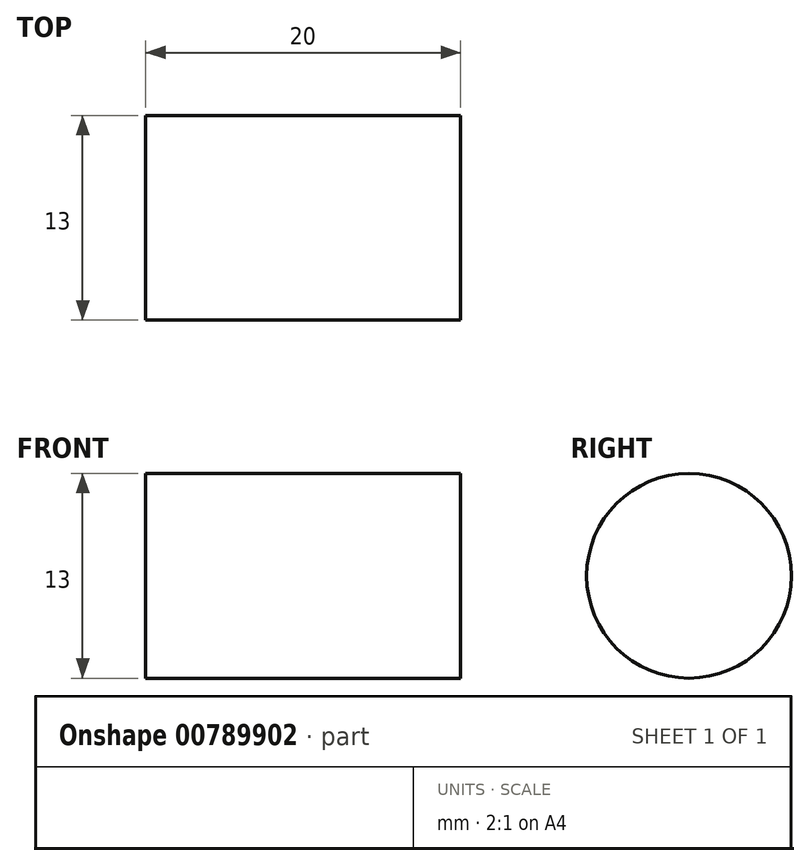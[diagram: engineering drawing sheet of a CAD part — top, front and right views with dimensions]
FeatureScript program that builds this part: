
annotation { "Feature Type Name" : "Feature", "Feature Type Description" : "" }
export const myFeature = defineFeature(function(context is Context, id is Id, definition is map)
    precondition{}
    {
        {
            var Q0;
            Q0=qCreatedBy(makeId("Right.planeOp"),FACE);
            var sketch = newSketch(context, id + "F0", { "sketchPlane" : qUnion([Q0])});
            skCircle(sketch, "E0", {"center": v(2086.78, 2239.07) * mm, "radius": 50 * mm, "construction": true});
            skCircle(sketch, "E1", {"center": v(2351, 2449) * mm, "radius": 2.12 * mm, "construction": true});
            skCircle(sketch, "E2", {"center": v(2325.71, 2465.14) * mm, "radius": 2.12 * mm, "construction": true});
            skCircle(sketch, "E3", {"center": v(2435.8, 2760.38) * mm, "radius": 2.12 * mm, "construction": true});
            skCircle(sketch, "E4", {"center": v(2431.3, 2790.04) * mm, "radius": 2.12 * mm, "construction": true});
            skCircle(sketch, "E5", {"center": v(2579.07, 2770.86) * mm, "radius": 5.5 * mm, "construction": true});
            skCircle(sketch, "E6", {"center": v(2661.57, 2688.36) * mm, "radius": 5.5 * mm, "construction": true});
            skCircle(sketch, "E7", {"center": v(2637.4, 2746.7) * mm, "radius": 5.5 * mm, "construction": true});
            skCircle(sketch, "E8", {"center": v(2520.73, 2746.7) * mm, "radius": 5.5 * mm, "construction": true});
            skCircle(sketch, "E9", {"center": v(2520.73, 2630.03) * mm, "radius": 5.5 * mm, "construction": true});
            skCircle(sketch, "E10", {"center": v(2496.57, 2688.36) * mm, "radius": 5.5 * mm, "construction": true});
            skCircle(sketch, "E11", {"center": v(2579.07, 2605.86) * mm, "radius": 5.5 * mm, "construction": true});
            skCircle(sketch, "E12", {"center": v(2637.4, 2630.03) * mm, "radius": 5.5 * mm, "construction": true});
            skCircle(sketch, "E13", {"center": v(2427.07, 2409.36) * mm, "radius": 10 * mm, "construction": true});
            skCircle(sketch, "E14", {"center": v(2622.07, 2789.36) * mm, "radius": 11 * mm, "construction": true});
            skCircle(sketch, "E15", {"center": v(2652.07, 2789.36) * mm, "radius": 6.5 * mm, "construction": true});
            skCircle(sketch, "E16", {"center": v(2102.07, 2789.36) * mm, "radius": 6.5 * mm, "construction": true});
            skCircle(sketch, "E17", {"center": v(2102.07, 2394.36) * mm, "radius": 6.5 * mm, "construction": true});
            skCircle(sketch, "E18", {"center": v(2217.07, 2764.36) * mm, "radius": 4.5 * mm, "construction": true});
            skArc(sketch, "E19", {"start": v(2079.57, 2594.36) * mm, "mid": v(2077.8, 2590.1) * mm, "end": v(2082.07, 2591.86) * mm, "construction": true});
            skLineSegment(sketch, "E20", {"start": v(2075.94, 2591.86) * mm, "end": v(2083.2, 2591.86) * mm, "construction": true});
            skLineSegment(sketch, "E21", {"start": v(2079.57, 2595.49) * mm, "end": v(2079.57, 2588.24) * mm, "construction": true});
            skCircle(sketch, "E22", {"center": v(2079.57, 2591.86) * mm, "radius": 2.12 * mm, "construction": true});
            skArc(sketch, "E23", {"start": v(2084.7, 2379.49) * mm, "mid": v(2082.92, 2375.22) * mm, "end": v(2087.2, 2376.99) * mm, "construction": true});
            skLineSegment(sketch, "E24", {"start": v(2081.07, 2376.99) * mm, "end": v(2088.32, 2376.99) * mm, "construction": true});
            skLineSegment(sketch, "E25", {"start": v(2084.7, 2380.61) * mm, "end": v(2084.7, 2373.36) * mm, "construction": true});
            skCircle(sketch, "E26", {"center": v(2084.7, 2376.99) * mm, "radius": 2.12 * mm, "construction": true});
            skArc(sketch, "E27", {"start": v(2463.4, 2375.7) * mm, "mid": v(2461.64, 2371.43) * mm, "end": v(2465.9, 2373.2) * mm, "construction": true});
            skLineSegment(sketch, "E28", {"start": v(2459.78, 2373.2) * mm, "end": v(2467.03, 2373.2) * mm, "construction": true});
            skLineSegment(sketch, "E29", {"start": v(2463.4, 2376.82) * mm, "end": v(2463.4, 2369.57) * mm, "construction": true});
            skCircle(sketch, "E30", {"center": v(2463.4, 2373.2) * mm, "radius": 2.12 * mm, "construction": true});
            skArc(sketch, "E31", {"start": v(2569.26, 2479.66) * mm, "mid": v(2567.5, 2475.4) * mm, "end": v(2571.76, 2477.16) * mm, "construction": true});
            skLineSegment(sketch, "E32", {"start": v(2565.64, 2477.16) * mm, "end": v(2572.89, 2477.16) * mm, "construction": true});
            skLineSegment(sketch, "E33", {"start": v(2569.26, 2480.79) * mm, "end": v(2569.26, 2473.54) * mm, "construction": true});
            skCircle(sketch, "E34", {"center": v(2569.26, 2477.16) * mm, "radius": 2.12 * mm, "construction": true});
            skArc(sketch, "E35", {"start": v(2673.23, 2585.52) * mm, "mid": v(2671.47, 2581.25) * mm, "end": v(2675.73, 2583.02) * mm, "construction": true});
            skLineSegment(sketch, "E36", {"start": v(2669.6, 2583.02) * mm, "end": v(2676.86, 2583.02) * mm, "construction": true});
            skLineSegment(sketch, "E37", {"start": v(2673.23, 2586.64) * mm, "end": v(2673.23, 2579.4) * mm, "construction": true});
            skCircle(sketch, "E38", {"center": v(2673.23, 2583.02) * mm, "radius": 2.12 * mm, "construction": true});
            skArc(sketch, "E39", {"start": v(2669.44, 2809.24) * mm, "mid": v(2667.67, 2804.97) * mm, "end": v(2671.94, 2806.74) * mm, "construction": true});
            skLineSegment(sketch, "E40", {"start": v(2665.81, 2806.74) * mm, "end": v(2673.06, 2806.74) * mm, "construction": true});
            skLineSegment(sketch, "E41", {"start": v(2669.44, 2810.36) * mm, "end": v(2669.44, 2803.11) * mm, "construction": true});
            skCircle(sketch, "E42", {"center": v(2669.44, 2806.74) * mm, "radius": 2.12 * mm, "construction": true});
            skArc(sketch, "E43", {"start": v(2474.44, 2814.36) * mm, "mid": v(2472.67, 2810.1) * mm, "end": v(2476.94, 2811.86) * mm, "construction": true});
            skLineSegment(sketch, "E44", {"start": v(2470.81, 2811.86) * mm, "end": v(2478.06, 2811.86) * mm, "construction": true});
            skLineSegment(sketch, "E45", {"start": v(2474.44, 2815.49) * mm, "end": v(2474.44, 2808.24) * mm, "construction": true});
            skCircle(sketch, "E46", {"center": v(2474.44, 2811.86) * mm, "radius": 2.12 * mm, "construction": true});
            skArc(sketch, "E47", {"start": v(2279.7, 2814.36) * mm, "mid": v(2277.92, 2810.1) * mm, "end": v(2282.2, 2811.86) * mm, "construction": true});
            skLineSegment(sketch, "E48", {"start": v(2276.07, 2811.86) * mm, "end": v(2283.32, 2811.86) * mm, "construction": true});
            skLineSegment(sketch, "E49", {"start": v(2279.7, 2815.49) * mm, "end": v(2279.7, 2808.24) * mm, "construction": true});
            skCircle(sketch, "E50", {"center": v(2279.7, 2811.86) * mm, "radius": 2.12 * mm, "construction": true});
            skArc(sketch, "E51", {"start": v(2084.7, 2809.24) * mm, "mid": v(2082.92, 2804.97) * mm, "end": v(2087.2, 2806.74) * mm, "construction": true});
            skLineSegment(sketch, "E52", {"start": v(2081.07, 2806.74) * mm, "end": v(2088.32, 2806.74) * mm, "construction": true});
            skLineSegment(sketch, "E53", {"start": v(2084.7, 2810.36) * mm, "end": v(2084.7, 2803.11) * mm, "construction": true});
            skCircle(sketch, "E54", {"center": v(2084.7, 2806.74) * mm, "radius": 2.12 * mm, "construction": true});
            skCircle(sketch, "E55", {"center": v(2579.07, 2688.36) * mm, "radius": 55 * mm, "construction": true});
            skLineSegment(sketch, "E56", {"start": v(2318.05, 2494.04) * mm, "end": v(2326.48, 2488.66) * mm, "construction": true});
            skArc(sketch, "E57", {"start": v(2323.13, 2496.43) * mm, "mid": v(2320.87, 2496.83) * mm, "end": v(2319, 2495.51) * mm, "construction": true});
            skLineSegment(sketch, "E58", {"start": v(2327.7, 2490.56) * mm, "end": v(2319.63, 2477.91) * mm, "construction": true});
            skLineSegment(sketch, "E59", {"start": v(2296.28, 2459.9) * mm, "end": v(2304.7, 2454.51) * mm, "construction": true});
            skArc(sketch, "E60", {"start": v(2295.34, 2458.42) * mm, "mid": v(2294.94, 2456.15) * mm, "end": v(2296.25, 2454.27) * mm, "construction": true});
            skLineSegment(sketch, "E61", {"start": v(2311.56, 2465.26) * mm, "end": v(2303.5, 2452.62) * mm, "construction": true});
            skLineSegment(sketch, "E62", {"start": v(2295.34, 2458.42) * mm, "end": v(2319, 2495.51) * mm, "construction": true});
            skLineSegment(sketch, "E63", {"start": v(2301.92, 2468.74) * mm, "end": v(2310.35, 2463.37) * mm, "construction": true});
            skLineSegment(sketch, "E64", {"start": v(2312.4, 2485.19) * mm, "end": v(2320.84, 2479.8) * mm, "construction": true});
            skLineSegment(sketch, "E65", {"start": v(2319.63, 2477.91) * mm, "end": v(2358.41, 2453.18) * mm, "construction": true});
            skLineSegment(sketch, "E66", {"start": v(2327.7, 2490.56) * mm, "end": v(2366.48, 2465.83) * mm, "construction": true});
            skLineSegment(sketch, "E67", {"start": v(2323.13, 2496.43) * mm, "end": v(2368.67, 2467.4) * mm, "construction": true});
            skLineSegment(sketch, "E68", {"start": v(2358.41, 2453.18) * mm, "end": v(2366.48, 2465.83) * mm, "construction": true});
            skArc(sketch, "E69", {"start": v(2369.58, 2463.26) * mm, "mid": v(2369.98, 2465.52) * mm, "end": v(2368.67, 2467.4) * mm, "construction": true});
            skLineSegment(sketch, "E70", {"start": v(2342.28, 2427.89) * mm, "end": v(2350.35, 2440.53) * mm, "construction": true});
            skLineSegment(sketch, "E71", {"start": v(2303.5, 2452.62) * mm, "end": v(2342.28, 2427.89) * mm, "construction": true});
            skLineSegment(sketch, "E72", {"start": v(2311.56, 2465.26) * mm, "end": v(2350.35, 2440.53) * mm, "construction": true});
            skLineSegment(sketch, "E73", {"start": v(2296.25, 2454.27) * mm, "end": v(2341.78, 2425.24) * mm, "construction": true});
            skLineSegment(sketch, "E74", {"start": v(2345.93, 2426.16) * mm, "end": v(2369.58, 2463.26) * mm, "construction": true});
            skArc(sketch, "E75", {"start": v(2341.78, 2425.24) * mm, "mid": v(2344.04, 2424.84) * mm, "end": v(2345.93, 2426.16) * mm, "construction": true});
            skLineSegment(sketch, "E76", {"start": v(2419.07, 2735.6) * mm, "end": v(2417.57, 2745.49) * mm, "construction": true});
            skArc(sketch, "E77", {"start": v(2413.92, 2737.85) * mm, "mid": v(2415.1, 2735.89) * mm, "end": v(2417.33, 2735.34) * mm, "construction": true});
            skLineSegment(sketch, "E78", {"start": v(2415.34, 2745.15) * mm, "end": v(2430.17, 2747.4) * mm, "construction": true});
            skLineSegment(sketch, "E79", {"start": v(2459.1, 2741.66) * mm, "end": v(2457.61, 2751.55) * mm, "construction": true});
            skArc(sketch, "E80", {"start": v(2460.84, 2741.93) * mm, "mid": v(2462.8, 2743.11) * mm, "end": v(2463.36, 2745.34) * mm, "construction": true});
            skLineSegment(sketch, "E81", {"start": v(2445, 2749.64) * mm, "end": v(2459.83, 2751.89) * mm, "construction": true});
            skLineSegment(sketch, "E82", {"start": v(2460.84, 2741.93) * mm, "end": v(2417.33, 2735.34) * mm, "construction": true});
            skLineSegment(sketch, "E83", {"start": v(2448.73, 2740.1) * mm, "end": v(2447.23, 2749.98) * mm, "construction": true});
            skLineSegment(sketch, "E84", {"start": v(2429.45, 2737.17) * mm, "end": v(2427.95, 2747.06) * mm, "construction": true});
            skLineSegment(sketch, "E85", {"start": v(2430.17, 2747.4) * mm, "end": v(2423.28, 2792.88) * mm, "construction": true});
            skLineSegment(sketch, "E86", {"start": v(2415.34, 2745.15) * mm, "end": v(2408.45, 2790.63) * mm, "construction": true});
            skLineSegment(sketch, "E87", {"start": v(2413.92, 2737.85) * mm, "end": v(2405.83, 2791.24) * mm, "construction": true});
            skLineSegment(sketch, "E88", {"start": v(2423.28, 2792.88) * mm, "end": v(2408.45, 2790.63) * mm, "construction": true});
            skArc(sketch, "E89", {"start": v(2408.35, 2794.66) * mm, "mid": v(2406.38, 2793.47) * mm, "end": v(2405.83, 2791.24) * mm, "construction": true});
            skLineSegment(sketch, "E90", {"start": v(2452.94, 2797.37) * mm, "end": v(2438.11, 2795.12) * mm, "construction": true});
            skLineSegment(sketch, "E91", {"start": v(2459.83, 2751.89) * mm, "end": v(2452.94, 2797.37) * mm, "construction": true});
            skLineSegment(sketch, "E92", {"start": v(2445, 2749.64) * mm, "end": v(2438.11, 2795.12) * mm, "construction": true});
            skLineSegment(sketch, "E93", {"start": v(2463.36, 2745.34) * mm, "end": v(2455.27, 2798.73) * mm, "construction": true});
            skLineSegment(sketch, "E94", {"start": v(2451.85, 2801.25) * mm, "end": v(2408.35, 2794.66) * mm, "construction": true});
            skArc(sketch, "E95", {"start": v(2455.27, 2798.73) * mm, "mid": v(2454.08, 2800.7) * mm, "end": v(2451.85, 2801.25) * mm, "construction": true});
            skArc(sketch, "E96", {"start": v(2207.17, 2779.23) * mm, "mid": v(2162.07, 2764.36) * mm, "end": v(2207.17, 2749.5) * mm, "construction": true});
            skCircle(sketch, "E97", {"center": v(2187.07, 2764.36) * mm, "radius": 14 * mm, "construction": true});
            skLineSegment(sketch, "E98", {"start": v(2484.93, 2814.36) * mm, "end": v(2657.07, 2814.36) * mm, "construction": true});
            skLineSegment(sketch, "E99", {"start": v(2290.18, 2814.36) * mm, "end": v(2463.95, 2814.36) * mm, "construction": true});
            skArc(sketch, "E100", {"start": v(2466.95, 2811.5) * mm, "mid": v(2474.44, 2804.36) * mm, "end": v(2481.93, 2811.5) * mm, "construction": true});
            skArc(sketch, "E101", {"start": v(2484.93, 2814.36) * mm, "mid": v(2482.86, 2813.53) * mm, "end": v(2481.93, 2811.5) * mm, "construction": true});
            skArc(sketch, "E102", {"start": v(2466.95, 2811.5) * mm, "mid": v(2466.02, 2813.53) * mm, "end": v(2463.95, 2814.36) * mm, "construction": true});
            skArc(sketch, "E103", {"start": v(2272.2, 2811.5) * mm, "mid": v(2271.27, 2813.53) * mm, "end": v(2269.2, 2814.36) * mm, "construction": true});
            skArc(sketch, "E104", {"start": v(2290.18, 2814.36) * mm, "mid": v(2288.1, 2813.53) * mm, "end": v(2287.18, 2811.5) * mm, "construction": true});
            skArc(sketch, "E105", {"start": v(2285.24, 2806.81) * mm, "mid": v(2286.62, 2809) * mm, "end": v(2287.18, 2811.5) * mm, "construction": true});
            skArc(sketch, "E106", {"start": v(2272.2, 2811.5) * mm, "mid": v(2279.7, 2804.36) * mm, "end": v(2287.18, 2811.5) * mm, "construction": true});
            skLineSegment(sketch, "E107", {"start": v(2455.9, 2373.2) * mm, "end": v(2455.9, 2372.36) * mm, "construction": true});
            skLineSegment(sketch, "E108", {"start": v(2092.2, 2376.99) * mm, "end": v(2092.2, 2372.36) * mm, "construction": true});
            skArc(sketch, "E109", {"start": v(2574.3, 2482.71) * mm, "mid": v(2563.96, 2482.47) * mm, "end": v(2563.71, 2472.12) * mm, "construction": true});
            skLineSegment(sketch, "E110", {"start": v(2077.07, 2510.77) * mm, "end": v(2077.07, 2389.36) * mm, "construction": true});
            skLineSegment(sketch, "E111", {"start": v(2077.07, 2714.11) * mm, "end": v(2077.07, 2602.35) * mm, "construction": true});
            skArc(sketch, "E112", {"start": v(2662.63, 2809.87) * mm, "mid": v(2662.55, 2812.52) * mm, "end": v(2660.4, 2814.08) * mm, "construction": true});
            skArc(sketch, "E113", {"start": v(2676.79, 2797.7) * mm, "mid": v(2675.23, 2799.85) * mm, "end": v(2672.57, 2799.92) * mm, "construction": true});
            skArc(sketch, "E114", {"start": v(2660.4, 2814.08) * mm, "mid": v(2658.74, 2814.3) * mm, "end": v(2657.07, 2814.36) * mm, "construction": true});
            skArc(sketch, "E115", {"start": v(2662.63, 2809.87) * mm, "mid": v(2664.14, 2801.43) * mm, "end": v(2672.57, 2799.92) * mm, "construction": true});
            skArc(sketch, "E116", {"start": v(2677.07, 2794.36) * mm, "mid": v(2677, 2796.04) * mm, "end": v(2676.79, 2797.7) * mm, "construction": true});
            skArc(sketch, "E117", {"start": v(2682.07, 2794.36) * mm, "mid": v(2674.74, 2812.04) * mm, "end": v(2657.07, 2819.36) * mm, "construction": true});
            skArc(sketch, "E118", {"start": v(2079.92, 2584.37) * mm, "mid": v(2077.9, 2583.44) * mm, "end": v(2077.07, 2581.37) * mm, "construction": true});
            skArc(sketch, "E119", {"start": v(2077.07, 2602.35) * mm, "mid": v(2077.9, 2600.28) * mm, "end": v(2079.92, 2599.35) * mm, "construction": true});
            skLineSegment(sketch, "E120", {"start": v(2077.07, 2581.37) * mm, "end": v(2077.07, 2510.77) * mm, "construction": true});
            skArc(sketch, "E121", {"start": v(2079.92, 2584.37) * mm, "mid": v(2087.07, 2591.86) * mm, "end": v(2079.92, 2599.35) * mm, "construction": true});
            skArc(sketch, "E122", {"start": v(2097.07, 2819.36) * mm, "mid": v(2079.39, 2812.04) * mm, "end": v(2072.07, 2794.36) * mm, "construction": true});
            skArc(sketch, "E123", {"start": v(2077.35, 2797.7) * mm, "mid": v(2077.14, 2796.04) * mm, "end": v(2077.07, 2794.36) * mm, "construction": true});
            skArc(sketch, "E124", {"start": v(2081.56, 2799.92) * mm, "mid": v(2090, 2801.43) * mm, "end": v(2091.5, 2809.87) * mm, "construction": true});
            skArc(sketch, "E125", {"start": v(2097.07, 2814.36) * mm, "mid": v(2095.4, 2814.3) * mm, "end": v(2093.73, 2814.08) * mm, "construction": true});
            skArc(sketch, "E126", {"start": v(2081.56, 2799.92) * mm, "mid": v(2078.9, 2799.85) * mm, "end": v(2077.35, 2797.7) * mm, "construction": true});
            skArc(sketch, "E127", {"start": v(2093.73, 2814.08) * mm, "mid": v(2091.58, 2812.52) * mm, "end": v(2091.5, 2809.87) * mm, "construction": true});
            skArc(sketch, "E128", {"start": v(2077.35, 2386.03) * mm, "mid": v(2078.9, 2383.87) * mm, "end": v(2081.56, 2383.8) * mm, "construction": true});
            skArc(sketch, "E129", {"start": v(2092.2, 2376.99) * mm, "mid": v(2088.74, 2383.3) * mm, "end": v(2081.56, 2383.8) * mm, "construction": true});
            skArc(sketch, "E130", {"start": v(2563.61, 2467.98) * mm, "mid": v(2564.5, 2470.03) * mm, "end": v(2563.71, 2472.12) * mm, "construction": true});
            skArc(sketch, "E131", {"start": v(2574.3, 2482.71) * mm, "mid": v(2576.4, 2481.94) * mm, "end": v(2578.45, 2482.81) * mm, "construction": true});
            skLineSegment(sketch, "E132", {"start": v(2578.45, 2482.81) * mm, "end": v(2668.54, 2572.9) * mm, "construction": true});
            skArc(sketch, "E133", {"start": v(2469.11, 2378.06) * mm, "mid": v(2471.28, 2377) * mm, "end": v(2473.52, 2377.89) * mm, "construction": true});
            skArc(sketch, "E134", {"start": v(2469.11, 2378.06) * mm, "mid": v(2460.54, 2380.12) * mm, "end": v(2455.93, 2372.6) * mm, "construction": true});
            skArc(sketch, "E135", {"start": v(2668.54, 2572.9) * mm, "mid": v(2669.42, 2575.15) * mm, "end": v(2668.37, 2577.31) * mm, "construction": true});
            skArc(sketch, "E136", {"start": v(2673.83, 2590.5) * mm, "mid": v(2676.1, 2591.28) * mm, "end": v(2677.07, 2593.49) * mm, "construction": true});
            skArc(sketch, "E137", {"start": v(2673.83, 2590.5) * mm, "mid": v(2666.3, 2585.9) * mm, "end": v(2668.37, 2577.31) * mm, "construction": true});
            skLineSegment(sketch, "E138", {"start": v(2677.07, 2663.74) * mm, "end": v(2677.07, 2794.36) * mm, "construction": true});
            skLineSegment(sketch, "E139", {"start": v(2193.07, 2814.36) * mm, "end": v(2269.2, 2814.36) * mm, "construction": true});
            skArc(sketch, "E140", {"start": v(2077.07, 2389.36) * mm, "mid": v(2077.14, 2387.69) * mm, "end": v(2077.35, 2386.03) * mm, "construction": true});
            skLineSegment(sketch, "E141", {"start": v(2097.07, 2814.36) * mm, "end": v(2193.07, 2814.36) * mm, "construction": true});
            skLineSegment(sketch, "E142", {"start": v(2677.07, 2593.49) * mm, "end": v(2677.07, 2663.74) * mm, "construction": true});
            skLineSegment(sketch, "E143", {"start": v(2473.52, 2377.89) * mm, "end": v(2563.61, 2467.98) * mm, "construction": true});
            skLineSegment(sketch, "E144", {"start": v(2077.07, 2794.36) * mm, "end": v(2077.07, 2714.11) * mm, "construction": true});
            skArc(sketch, "E145", {"start": v(2072.07, 2389.36) * mm, "mid": v(2079.39, 2371.68) * mm, "end": v(2097.07, 2364.36) * mm, "construction": true});
            skArc(sketch, "E146", {"start": v(2674.74, 2572.04) * mm, "mid": v(2680.16, 2580.15) * mm, "end": v(2682.07, 2589.72) * mm, "construction": true});
            skLineSegment(sketch, "E147", {"start": v(2456.71, 2364.36) * mm, "end": v(2097.07, 2364.36) * mm, "construction": true});
            skLineSegment(sketch, "E148", {"start": v(2474.39, 2371.68) * mm, "end": v(2674.74, 2572.04) * mm, "construction": true});
            skLineSegment(sketch, "E149", {"start": v(2682.07, 2589.72) * mm, "end": v(2682.07, 2794.36) * mm, "construction": true});
            skCircle(sketch, "E150", {"center": v(2327.07, 2604.36) * mm, "radius": 102.5 * mm, "construction": true});
            skCircle(sketch, "E151", {"center": v(2182.07, 2459.36) * mm, "radius": 25 * mm, "construction": true});
            skLineSegment(sketch, "E152", {"start": v(2072.07, 2794.36) * mm, "end": v(2072.07, 2389.36) * mm, "construction": true});
            skLineSegment(sketch, "E153", {"start": v(2097.07, 2819.36) * mm, "end": v(2657.07, 2819.36) * mm, "construction": true});
            skLineSegment(sketch, "E154", {"start": v(2452.9, 2369.36) * mm, "end": v(2095.2, 2369.36) * mm, "construction": true});
            skArc(sketch, "E155", {"start": v(2452.9, 2369.36) * mm, "mid": v(2455.03, 2370.24) * mm, "end": v(2455.9, 2372.36) * mm, "construction": true});
            skArc(sketch, "E156", {"start": v(2092.2, 2372.36) * mm, "mid": v(2093.07, 2370.24) * mm, "end": v(2095.2, 2369.36) * mm, "construction": true});
            skArc(sketch, "E157", {"start": v(2456.71, 2364.36) * mm, "mid": v(2466.28, 2366.26) * mm, "end": v(2474.39, 2371.68) * mm, "construction": true});
            skLineSegment(sketch, "E158", {"start": v(2207.17, 2779.23) * mm, "end": v(2207.17, 2749.5) * mm, "construction": true});
            skCircle(sketch, "E159", {"center": v(-302.16, -273.88) * mm, "radius": 50 * mm, "construction": true});
            skLineSegment(sketch, "E160", {"start": v(85.75, 157.25) * mm, "end": v(85.75, 169) * mm, "construction": true});
            skLineSegment(sketch, "E161", {"start": v(101.75, 157.25) * mm, "end": v(101.75, 169) * mm, "construction": true});
            skLineSegment(sketch, "E162", {"start": v(-254, -118.93) * mm, "end": v(-257.54, -122.46) * mm, "construction": true});
            skLineSegment(sketch, "E163", {"start": v(-296.43, -76.5) * mm, "end": v(-299.96, -80.04) * mm, "construction": true});
            skCircle(sketch, "E164", {"center": v(225, -180) * mm, "radius": 3.25 * mm, "construction": true});
            skCircle(sketch, "E165", {"center": v(110, 160) * mm, "radius": 6.5 * mm});
            skCircle(sketch, "E166", {"center": v(225, 185) * mm, "radius": 6.5 * mm});
            skCircle(sketch, "E167", {"center": v(225, -210) * mm, "radius": 6.5 * mm});
            skCircle(sketch, "E168", {"center": v(-100, -195) * mm, "radius": 10 * mm});
            skCircle(sketch, "E169", {"center": v(-260, 191) * mm, "radius": 11 * mm});
            skCircle(sketch, "E170", {"center": v(-325, 185) * mm, "radius": 6.5 * mm});
            skCircle(sketch, "E171", {"center": v(-290, 191) * mm, "radius": 11 * mm});
            skCircle(sketch, "E172", {"center": v(15, -165) * mm, "radius": 20 * mm});
            skCircle(sketch, "E173", {"center": v(165, 15) * mm, "radius": 20 * mm});
            skCircle(sketch, "E174", {"center": v(-346.17, -21.34) * mm, "radius": 2.12 * mm, "construction": true});
            skLineSegment(sketch, "E175", {"start": v(-346.17, -17.72) * mm, "end": v(-346.17, -24.97) * mm, "construction": true});
            skLineSegment(sketch, "E176", {"start": v(-349.8, -21.34) * mm, "end": v(-342.54, -21.34) * mm, "construction": true});
            skCircle(sketch, "E177", {"center": v(-242.2, -127.2) * mm, "radius": 2.12 * mm, "construction": true});
            skLineSegment(sketch, "E178", {"start": v(-242.2, -123.57) * mm, "end": v(-242.2, -130.82) * mm, "construction": true});
            skLineSegment(sketch, "E179", {"start": v(-245.82, -127.2) * mm, "end": v(-238.57, -127.2) * mm, "construction": true});
            skCircle(sketch, "E180", {"center": v(-136.34, -231.17) * mm, "radius": 2.12 * mm, "construction": true});
            skLineSegment(sketch, "E181", {"start": v(-136.34, -227.54) * mm, "end": v(-136.34, -234.8) * mm, "construction": true});
            skLineSegment(sketch, "E182", {"start": v(-139.97, -231.17) * mm, "end": v(-132.72, -231.17) * mm, "construction": true});
            skCircle(sketch, "E183", {"center": v(242.37, -227.37) * mm, "radius": 2.12 * mm, "construction": true});
            skLineSegment(sketch, "E184", {"start": v(242.37, -223.75) * mm, "end": v(242.37, -231) * mm, "construction": true});
            skLineSegment(sketch, "E185", {"start": v(238.75, -227.37) * mm, "end": v(246, -227.37) * mm, "construction": true});
            skCircle(sketch, "E186", {"center": v(247.5, -12.5) * mm, "radius": 2.12 * mm, "construction": true});
            skLineSegment(sketch, "E187", {"start": v(247.5, -8.88) * mm, "end": v(247.5, -16.13) * mm, "construction": true});
            skLineSegment(sketch, "E188", {"start": v(243.88, -12.5) * mm, "end": v(251.13, -12.5) * mm, "construction": true});
            skCircle(sketch, "E189", {"center": v(242.37, 202.37) * mm, "radius": 2.12 * mm, "construction": true});
            skLineSegment(sketch, "E190", {"start": v(242.37, 206) * mm, "end": v(242.37, 198.75) * mm, "construction": true});
            skLineSegment(sketch, "E191", {"start": v(238.75, 202.37) * mm, "end": v(246, 202.37) * mm, "construction": true});
            skCircle(sketch, "E192", {"center": v(47.37, 207.5) * mm, "radius": 2.12 * mm, "construction": true});
            skLineSegment(sketch, "E193", {"start": v(47.37, 211.12) * mm, "end": v(47.37, 203.87) * mm, "construction": true});
            skLineSegment(sketch, "E194", {"start": v(43.75, 207.5) * mm, "end": v(51, 207.5) * mm, "construction": true});
            skCircle(sketch, "E195", {"center": v(-147.37, 207.5) * mm, "radius": 2.12 * mm, "construction": true});
            skLineSegment(sketch, "E196", {"start": v(-147.37, 211.12) * mm, "end": v(-147.37, 203.87) * mm, "construction": true});
            skLineSegment(sketch, "E197", {"start": v(-151, 207.5) * mm, "end": v(-143.75, 207.5) * mm, "construction": true});
            skLineSegment(sketch, "E198", {"start": v(-346, 202.37) * mm, "end": v(-338.75, 202.37) * mm, "construction": true});
            skLineSegment(sketch, "E199", {"start": v(-342.37, 206) * mm, "end": v(-342.37, 198.75) * mm, "construction": true});
            skCircle(sketch, "E200", {"center": v(-342.37, 202.37) * mm, "radius": 2.12 * mm, "construction": true});
            skCircle(sketch, "E201", {"center": v(-252, 84) * mm, "radius": 20 * mm});
            skLineSegment(sketch, "E202", {"start": v(-125.84, -235) * mm, "end": v(83, -235) * mm, "construction": true});
            skLineSegment(sketch, "E203", {"start": v(-261, 210) * mm, "end": v(-330, 210) * mm, "construction": true});
            skArc(sketch, "E204", {"start": v(1318.17, 2462.2) * mm, "mid": v(1311.96, 2465.98) * mm, "end": v(1305.73, 2469.73) * mm, "construction": true});
            skLineSegment(sketch, "E205", {"start": v(250, -93.6) * mm, "end": v(250, -215) * mm, "construction": true});
            skLineSegment(sketch, "E206", {"start": v(250, 109.75) * mm, "end": v(250, -2.01) * mm, "construction": true});
            skLineSegment(sketch, "E207", {"start": v(-157.86, 210) * mm, "end": v(-261, 210) * mm, "construction": true});
            skArc(sketch, "E208", {"start": v(1415.86, 2801.03) * mm, "mid": v(1415.38, 2801.27) * mm, "end": v(1414.9, 2801.51) * mm, "construction": true});
            skArc(sketch, "E209", {"start": v(1399.95, 2801.59) * mm, "mid": v(1398.22, 2802.64) * mm, "end": v(1396.5, 2803.68) * mm, "construction": true});
            skLineSegment(sketch, "E210", {"start": v(36.89, 210) * mm, "end": v(-136.89, 210) * mm, "construction": true});
            skArc(sketch, "E211", {"start": v(1594.7, 2801.59) * mm, "mid": v(1592.97, 2802.64) * mm, "end": v(1591.24, 2803.68) * mm, "construction": true});
            skArc(sketch, "E212", {"start": v(1610.61, 2801.03) * mm, "mid": v(1610.15, 2801.3) * mm, "end": v(1609.68, 2801.59) * mm, "construction": true});
            skArc(sketch, "E213", {"start": v(1207.2, 2786.51) * mm, "mid": v(1206.15, 2787.15) * mm, "end": v(1205.1, 2787.78) * mm, "construction": true});
            skArc(sketch, "E214", {"start": v(1223.81, 2802.77) * mm, "mid": v(1222.65, 2803.47) * mm, "end": v(1221.48, 2804.17) * mm, "construction": true});
            skArc(sketch, "E215", {"start": v(1207.2, 2780.04) * mm, "mid": v(1203.5, 2782.25) * mm, "end": v(1199.82, 2784.45) * mm, "construction": true});
            skArc(sketch, "E216", {"start": v(1804.82, 2571.46) * mm, "mid": v(1803.1, 2572.5) * mm, "end": v(1801.4, 2573.53) * mm, "construction": true});
            skLineSegment(sketch, "E217", {"start": v(250, -22.99) * mm, "end": v(250, -93.6) * mm, "construction": true});
            skArc(sketch, "E218", {"start": v(1809.82, 2784.45) * mm, "mid": v(1795.19, 2793.39) * mm, "end": v(1780.5, 2802.25) * mm, "construction": true});
            skArc(sketch, "E219", {"start": v(1804.82, 2784.45) * mm, "mid": v(1803.97, 2784.96) * mm, "end": v(1803.13, 2785.48) * mm, "construction": true});
            skArc(sketch, "E220", {"start": v(1787.4, 2802.9) * mm, "mid": v(1786.1, 2803.67) * mm, "end": v(1784.82, 2804.45) * mm, "construction": true});
            skArc(sketch, "E221", {"start": v(1804.4, 2787.54) * mm, "mid": v(1802.36, 2788.78) * mm, "end": v(1800.33, 2790) * mm, "construction": true});
            skArc(sketch, "E222", {"start": v(1790.38, 2799.95) * mm, "mid": v(1788.63, 2801.01) * mm, "end": v(1786.89, 2802.07) * mm, "construction": true});
            skArc(sketch, "E223", {"start": v(1794.46, 2364.2) * mm, "mid": v(1792.08, 2365.63) * mm, "end": v(1789.7, 2367.07) * mm, "construction": true});
            skArc(sketch, "E224", {"start": v(1424.59, 2361) * mm, "mid": v(1418.68, 2364.58) * mm, "end": v(1412.77, 2368.14) * mm, "construction": true});
            skArc(sketch, "E225", {"start": v(1213.52, 2567.4) * mm, "mid": v(1208.6, 2570.38) * mm, "end": v(1203.7, 2573.35) * mm, "construction": true});
            skLineSegment(sketch, "E226", {"start": v(134, 210) * mm, "end": v(57.86, 210) * mm, "construction": true});
            skArc(sketch, "E227", {"start": v(1804.54, 2376.11) * mm, "mid": v(1803.9, 2376.5) * mm, "end": v(1803.26, 2376.9) * mm, "construction": true});
            skLineSegment(sketch, "E228", {"start": v(230, 210) * mm, "end": v(134, 210) * mm, "construction": true});
            skLineSegment(sketch, "E229", {"start": v(-146.45, -226.48) * mm, "end": v(-236.55, -136.38) * mm, "construction": true});
            skLineSegment(sketch, "E230", {"start": v(250, 190) * mm, "end": v(250, 109.75) * mm, "construction": true});
            skLineSegment(sketch, "E231", {"start": v(-147.32, -232.68) * mm, "end": v(-347.68, -32.32) * mm, "construction": true});
            skLineSegment(sketch, "E232", {"start": v(-355, -14.64) * mm, "end": v(-355, 190) * mm, "construction": true});
            skCircle(sketch, "E233", {"center": v(145, -145) * mm, "radius": 25 * mm});
            skLineSegment(sketch, "E234", {"start": v(255, 190) * mm, "end": v(255, -215) * mm, "construction": true});
            skLineSegment(sketch, "E235", {"start": v(230, 215) * mm, "end": v(-330, 215) * mm, "construction": true});
            skLineSegment(sketch, "E236", {"start": v(15, -193) * mm, "end": v(15, -222) * mm, "construction": true});
            skLineSegment(sketch, "E237", {"start": v(-20, -190) * mm, "end": v(12, -190) * mm, "construction": true});
            skLineSegment(sketch, "E238", {"start": v(-55, -196) * mm, "end": v(-55, -222) * mm, "construction": true});
            skLineSegment(sketch, "E239", {"start": v(-128.84, -231.17) * mm, "end": v(-128.84, -232) * mm, "construction": true});
            skLineSegment(sketch, "E240", {"start": v(234.87, -227.37) * mm, "end": v(234.87, -232) * mm, "construction": true});
            skLineSegment(sketch, "E241", {"start": v(-129.64, -240) * mm, "end": v(230, -240) * mm, "construction": true});
            skLineSegment(sketch, "E242", {"start": v(-52.3, -225) * mm, "end": v(12, -225) * mm, "construction": true});
            skArc(sketch, "E243", {"start": v(1500.34, 2398.13) * mm, "mid": v(1500.08, 2398.29) * mm, "end": v(1499.82, 2398.45) * mm, "construction": true});
            skArc(sketch, "E244", {"start": v(1569.82, 2401.45) * mm, "mid": v(1568.06, 2402.51) * mm, "end": v(1566.3, 2403.58) * mm, "construction": true});
            skArc(sketch, "E245", {"start": v(1745.69, 2605.92) * mm, "mid": v(1745.25, 2606.18) * mm, "end": v(1744.82, 2606.45) * mm, "construction": true});
            skArc(sketch, "E246", {"start": v(1779.82, 2606.45) * mm, "mid": v(1778.06, 2607.51) * mm, "end": v(1776.3, 2608.58) * mm, "construction": true});
            skLineSegment(sketch, "E247", {"start": v(225, -52.3) * mm, "end": v(225, 12) * mm, "construction": true});
            skLineSegment(sketch, "E248", {"start": v(196, -55) * mm, "end": v(222, -55) * mm, "construction": true});
            skLineSegment(sketch, "E249", {"start": v(190, -20) * mm, "end": v(190, 12) * mm, "construction": true});
            skLineSegment(sketch, "E250", {"start": v(193, 15) * mm, "end": v(222, 15) * mm, "construction": true});
            skLineSegment(sketch, "E251", {"start": v(65.12, 80) * mm, "end": v(247, 80) * mm, "construction": true});
            skArc(sketch, "E252", {"start": v(1804.82, 2541.45) * mm, "mid": v(1803.06, 2542.51) * mm, "end": v(1801.3, 2543.58) * mm, "construction": true});
            skArc(sketch, "E253", {"start": v(1644.57, 2542.02) * mm, "mid": v(1643.95, 2542.4) * mm, "end": v(1643.34, 2542.77) * mm, "construction": true});
            skLineSegment(sketch, "E254", {"start": v(91.21, -50) * mm, "end": v(190.08, -50) * mm, "construction": true});
            skLineSegment(sketch, "E255", {"start": v(-50, -91.22) * mm, "end": v(-50, -190.08) * mm, "construction": true});
            skLineSegment(sketch, "E256", {"start": v(80, -65.12) * mm, "end": v(80, -232) * mm, "construction": true});
            skLineSegment(sketch, "E257", {"start": v(227.92, -50) * mm, "end": v(247, -50) * mm, "construction": true});
            skArc(sketch, "E258", {"start": v(1748.17, 2542.46) * mm, "mid": v(1746.54, 2543.46) * mm, "end": v(1744.9, 2544.45) * mm, "construction": true});
            skArc(sketch, "E259", {"start": v(1780.84, 2541.3) * mm, "mid": v(1780.3, 2541.63) * mm, "end": v(1779.78, 2541.95) * mm, "construction": true});
            skLineSegment(sketch, "E260", {"start": v(83, -235) * mm, "end": v(231.87, -235) * mm, "construction": true});
            skArc(sketch, "E261", {"start": v(1504.82, 2503.22) * mm, "mid": v(1503.7, 2503.9) * mm, "end": v(1502.58, 2504.58) * mm, "construction": true});
            skLineSegment(sketch, "E262", {"start": v(-50, -227.92) * mm, "end": v(-50, -232) * mm, "construction": true});
            skArc(sketch, "E263", {"start": v(1504.82, 2366.53) * mm, "mid": v(1503.25, 2367.48) * mm, "end": v(1501.68, 2368.43) * mm, "construction": true});
            skLineSegment(sketch, "E264", {"start": v(-20, -190) * mm, "end": v(-55, -196) * mm, "construction": true});
            skLineSegment(sketch, "E265", {"start": v(190, -20) * mm, "end": v(196, -55) * mm, "construction": true});
            skCircle(sketch, "E266", {"center": v(140, 160) * mm, "radius": 14 * mm});
            skArc(sketch, "E267", {"start": v(1675.4, 2738.13) * mm, "mid": v(1674.32, 2738.79) * mm, "end": v(1673.24, 2739.44) * mm, "construction": true});
            skArc(sketch, "E268", {"start": v(1674.82, 2761.45) * mm, "mid": v(1673.64, 2762.16) * mm, "end": v(1672.47, 2762.87) * mm, "construction": true});
            skArc(sketch, "E269", {"start": v(1635.4, 2761.1) * mm, "mid": v(1635.1, 2761.27) * mm, "end": v(1634.82, 2761.45) * mm, "construction": true});
            skLineSegment(sketch, "E270", {"start": v(80, 167) * mm, "end": v(80, 147) * mm, "construction": true});
            skLineSegment(sketch, "E271", {"start": v(120, 167) * mm, "end": v(120, 147) * mm, "construction": true});
            skArc(sketch, "E272", {"start": v(1675.55, 2738.36) * mm, "mid": v(1668.42, 2742.64) * mm, "end": v(1661.27, 2746.9) * mm, "construction": true});
            skLineSegment(sketch, "E273", {"start": v(82, 145) * mm, "end": v(118.42, 145) * mm, "construction": true});
            skLineSegment(sketch, "E274", {"start": v(118, 169) * mm, "end": v(82, 169) * mm, "construction": true});
            skCircle(sketch, "E275", {"center": v(0, 0) * mm, "radius": 102.5 * mm});
            skLineSegment(sketch, "E276", {"start": v(225, 12) * mm, "end": v(225, -28.79) * mm, "construction": true});
            skCircle(sketch, "E277", {"center": v(177, -160) * mm, "radius": 9 * mm});
            skLineSegment(sketch, "E278", {"start": v(255, 190) * mm, "end": v(255, -215) * mm});
            skLineSegment(sketch, "E279", {"start": v(255, -215) * mm, "end": v(230, -240) * mm});
            skLineSegment(sketch, "E280", {"start": v(-129.64, -240) * mm, "end": v(230, -240) * mm});
            skLineSegment(sketch, "E281", {"start": v(-129.64, -240) * mm, "end": v(-147.32, -232.68) * mm});
            skLineSegment(sketch, "E282", {"start": v(-147.32, -232.68) * mm, "end": v(-347.68, -32.32) * mm});
            skLineSegment(sketch, "E283", {"start": v(-347.68, -32.32) * mm, "end": v(-355, -14.64) * mm});
            skLineSegment(sketch, "E284", {"start": v(-355, -14.64) * mm, "end": v(-355, 190) * mm});
            skLineSegment(sketch, "E285", {"start": v(-355, 190) * mm, "end": v(-330, 215) * mm});
            skLineSegment(sketch, "E286", {"start": v(-330, 215) * mm, "end": v(230, 215) * mm});
            skLineSegment(sketch, "E287", {"start": v(230, 215) * mm, "end": v(255, 190) * mm});
            skSolve(sketch);
        }
        {
            var Q0;
            Q0=makeQuery(id+"F0.imprint","IMPRINT",FACE,{"disambiguationData":[TD([[makeQuery(id+"F0.imprint","IMPRINT",EDGE,{"derivedFrom":sQuery(id+"F0.wireOp",EDGE,"E165")}),1.0]])]});
            extrude(context, id + "F1", {"entities" : qUnion([Q0]), "depth" : 20 * mm, "offsetDistance" : 25 * mm});
        }
    });
